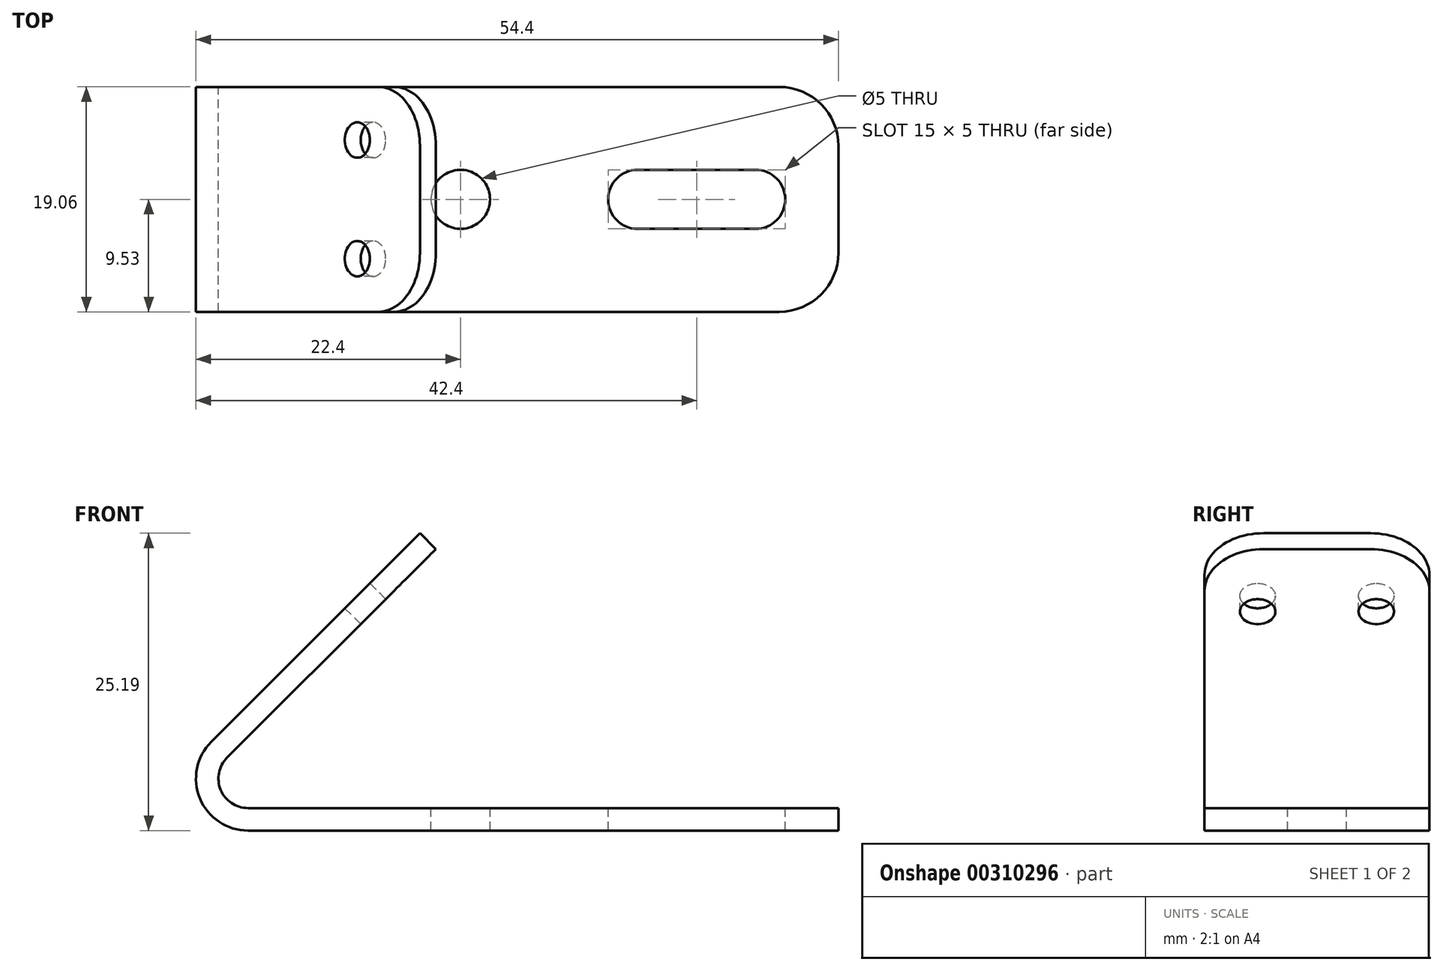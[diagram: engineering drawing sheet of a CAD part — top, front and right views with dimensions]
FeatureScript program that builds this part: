
annotation { "Feature Type Name" : "Feature", "Feature Type Description" : "" }
export const myFeature = defineFeature(function(context is Context, id is Id, definition is map)
    precondition{}
    {
        {
            var Q0;
            Q0=qCreatedBy(makeId("Front.planeOp"),FACE);
            var sketch = newSketch(context, id + "F0", { "sketchPlane" : qUnion([Q0])});
            skLineSegment(sketch, "E0", {"start": v(0, 0) * mm, "end": v(-50, 0) * mm});
            skLineSegment(sketch, "E1", {"start": v(-51.77, 4.27) * mm, "end": v(-34.1, 21.95) * mm});
            skLineSegment(sketch, "E2", {"start": v(-34.1, 21.95) * mm, "end": v(-35.43, 23.29) * mm});
            skLineSegment(sketch, "E3", {"start": v(-35.43, 23.29) * mm, "end": v(-53.11, 5.61) * mm});
            skLineSegment(sketch, "E4", {"start": v(-50, -1.9) * mm, "end": v(0, -1.9) * mm});
            skLineSegment(sketch, "E5", {"start": v(0, -1.9) * mm, "end": v(0, 0) * mm});
            skPoint(sketch, "E6.visualSharp", {"position": v(-56.04, 0) * mm});
            skArc(sketch, "E6.filletArc", {"start": v(-51.77, 4.27) * mm, "mid": v(-52.3, 1.54) * mm, "end": v(-50, 0) * mm});
            skPoint(sketch, "E7.visualSharp", {"position": v(-60.62, -1.9) * mm});
            skArc(sketch, "E7.filletArc", {"start": v(-53.11, 5.61) * mm, "mid": v(-54.07, 0.82) * mm, "end": v(-50, -1.9) * mm});
            skSolve(sketch);
        }
        {
            var Q0;
            Q0=makeQuery(id+"F0.imprint","IMPRINT",FACE,{"disambiguationData":[TD([[makeQuery(id+"F0.imprint","IMPRINT",EDGE,{"derivedFrom":sQuery(id+"F0.wireOp",EDGE,"E0")}),1.0]])]});
            extrude(context, id + "F1", {"entities" : qUnion([Q0]), "endBound" : BoundingType.SYMMETRIC, "depth" : 19.05 * mm});
        }
        {
            var Q0;
            Q0=makeQuery(id+"F1.opExtrude","SWEPT_FACE",FACE,{"disambiguationData":[OSD([sQuery(id+"F0.wireOp",EDGE,"E0")])]});
            var sketch = newSketch(context, id + "F2", { "sketchPlane" : qUnion([Q0])});
            skArc(sketch, "E8", {"start": v(-7, -2.5) * mm, "mid": v(-4.5, 0) * mm, "end": v(-7, 2.5) * mm});
            skArc(sketch, "E9", {"start": v(-17, 2.5) * mm, "mid": v(-19.5, 0) * mm, "end": v(-17, -2.5) * mm});
            skLineSegment(sketch, "E10", {"start": v(-17, 2.5) * mm, "end": v(-7, 2.5) * mm});
            skLineSegment(sketch, "E11", {"start": v(-17, -2.5) * mm, "end": v(-7, -2.5) * mm});
            skCircle(sketch, "E12", {"center": v(-32, 0) * mm, "radius": 2.5 * mm});
            skSolve(sketch);
        }
        {
            var Q0;
            Q0=makeQuery(id+"F2.imprint","IMPRINT",FACE,{"disambiguationData":[TD([[makeQuery(id+"F2.imprint","IMPRINT",EDGE,{"derivedFrom":sQuery(id+"F2.wireOp",EDGE,"E12")}),1.0]])]});
            var Q1;
            Q1=makeQuery(id+"F2.imprint","IMPRINT",FACE,{"disambiguationData":[TD([[makeQuery(id+"F2.imprint","IMPRINT",EDGE,{"derivedFrom":sQuery(id+"F2.wireOp",EDGE,"E8")}),1.0]])]});
            extrude(context, id + "F3", {"entities" : qUnion([Q0, Q1]), "operationType" : NewBodyOperationType.REMOVE, "oppositeDirection" : true, "depth" : 25 * mm});
        }
        {
            var Q0;
            Q0=makeQuery(id+"F1.opExtrude","SWEPT_FACE",FACE,{"disambiguationData":[OSD([sQuery(id+"F0.wireOp",EDGE,"E3")])]});
            var sketch = newSketch(context, id + "F4", { "sketchPlane" : qUnion([Q0])});
            skCircle(sketch, "E13", {"center": v(-5.03, -16.09) * mm, "radius": 1.5 * mm});
            skCircle(sketch, "E14", {"center": v(5.03, -16.09) * mm, "radius": 1.5 * mm});
            skSolve(sketch);
        }
        {
            var Q0;
            Q0=makeQuery(id+"F4.imprint","IMPRINT",FACE,{"disambiguationData":[TD([[makeQuery(id+"F4.imprint","IMPRINT",EDGE,{"derivedFrom":sQuery(id+"F4.wireOp",EDGE,"E13")}),1.0]])]});
            var Q1;
            Q1=makeQuery(id+"F4.imprint","IMPRINT",FACE,{"disambiguationData":[TD([[makeQuery(id+"F4.imprint","IMPRINT",EDGE,{"derivedFrom":sQuery(id+"F4.wireOp",EDGE,"E14")}),1.0]])]});
            var Q2;
            Q2=makeQuery(id+"F1.opExtrude","SWEPT_FACE",FACE,{"disambiguationData":[OSD([sQuery(id+"F0.wireOp",EDGE,"E1")])]});
            extrude(context, id + "F5", {"entities" : qUnion([Q0, Q1]), "operationType" : NewBodyOperationType.REMOVE, "endBound" : BoundingType.UP_TO_SURFACE, "oppositeDirection" : true, "endBoundEntityFace" : qUnion([Q2]), "depth" : 15 * mm});
        }
        {
            var Q0;
            Q0=makeQuery(id+"F1.opExtrude","CAP_EDGE",EDGE,{"disambiguationData":[OSD([sQuery(id+"F0.wireOp",EDGE,"E2")])],"isStart":false});
            var Q1;
            Q1=makeQuery(id+"F1.opExtrude","CAP_EDGE",EDGE,{"disambiguationData":[OSD([sQuery(id+"F0.wireOp",EDGE,"E2")])],"isStart":true});
            var Q2;
            Q2=makeQuery(id+"F1.opExtrude","CAP_EDGE",EDGE,{"disambiguationData":[OSD([sQuery(id+"F0.wireOp",EDGE,"E5")])],"isStart":false});
            var Q3;
            Q3=makeQuery(id+"F1.opExtrude","CAP_EDGE",EDGE,{"disambiguationData":[OSD([sQuery(id+"F0.wireOp",EDGE,"E5")])],"isStart":true});
            fillet(context, id + "F6", {"entities" : qUnion([Q0, Q1, Q2, Q3]), "radius" : 5 * mm, "tangentPropagation" : true, "allowEdgeOverflow" : false});
        }
    });
